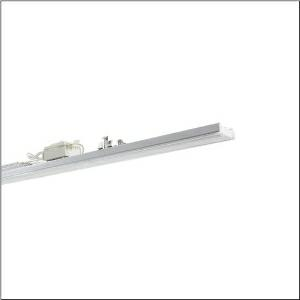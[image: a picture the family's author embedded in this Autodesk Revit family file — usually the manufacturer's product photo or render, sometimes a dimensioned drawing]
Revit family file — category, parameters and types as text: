
# Revit family: licross_r__21_recessed_ho_52tl1ede47xs_a4c3
name_source: partatom
category: Lighting Fixtures
units: mm (PartAtom-declared; Revit-internal decimal feet)

## family parameters
Cut with Voids When Loaded = No
Host = Face
Light Source = No
Part Type = Normal
Room Calculation Point = No
Round Connector Dimension = Use Diameter
Shared = No

## types (1)
- --- (1 x LED, 7310 lm, 44.1 W, 4000K)
    Apparent Load = 44 VA
    CIE Flux Codes = 85 95 99 100 100
    Color Rendering = 80
    Color Temperature = 4000K
    Default Elevation = 1800 mm
    Description = Licross® 21 Recessed HO, luminaire insert, of sheet steel, galvanised, coil coated, white, length: 750mm, width: 66mm, height: 67mm, LED rated luminous flux: 7.310lm, light colour: 840, control gear: DALI 2, with plug, 5-pole, with phase selection, mains connection: 220..240V, AC, 50/60Hz, rated input power: 44W, halogen-free wiring, primary light control with lens, of plastic, primary optical cover: cover, of PMMA, light emission: direct distribution, primary light characteristic: symmetric, protection rating (complete): IP40, insulation class (complete): insulation class I (protective earthing), certification: CE, ENEC, VDE, UKCA, protection symbol: D if used in an environment without relevant dust loads with corresponding accessories, impact resistance: IK06, permissible ambient temperature for indoor applications: -25..+30°C, corresponds to IFS (International Featured Standards) requirements for safety and quality in the food industry, reducing of maximum allowable ambient temperature of 5°C with ceiling mounting, LABS conformity tested according to VDMA 24364:2018-05, packaging unit: 1 piece
    Height = 58 mm
    Lamp = 1 x LED
    Lamp Light Flux = 7310 lm
    Lamp Power = 44.1 W
    Lamp count = 1
    Length = 750 mm
    Luminous efficacy = 166 lm/W
    Manufacturer = Siteco
    ModVariant = No
    Model = 52TL1EDE47XS
    Mounting Place = Ceiling
    Mounting Type = Pendant
    Number of Poles = 1
    OnlyDefault = Yes
    Power Factor = 1
    Product Name = Licross® 21 Recessed HO
    Product group = luminaire insert
    ProductGroupID = 902
    Protection Class = Protection class I
    Protection Degree = IP 40
    RLX_Detail_Level = 1
    RLX_Emergency_Light_Flux = 0 lm
    RLX_Emergency_Type = 0
    RLX_Emergency_Type_DB = No
    RlxData = <blob elided: 29541 chars, md5=e5db1ba1>
    Socket = socket
    Standby Power = 0 W
    System Light Flux = 7310 lm
    System Power = 44 W
    Type Comments = factory setting: luminous flux: 100 % | dim-lin: 254 | 484 mA
    Type Image = l_1296930.jpg
    URL = http://relux.com
    VarID = @adj_125632
    Voltage = 0 V
    Weight = 0.00 kg
    Width = 66 mm

## geometry (parser evidence)
native form markers: Blend x4, Sweep x9
no freeform markers — native parametric forms only
